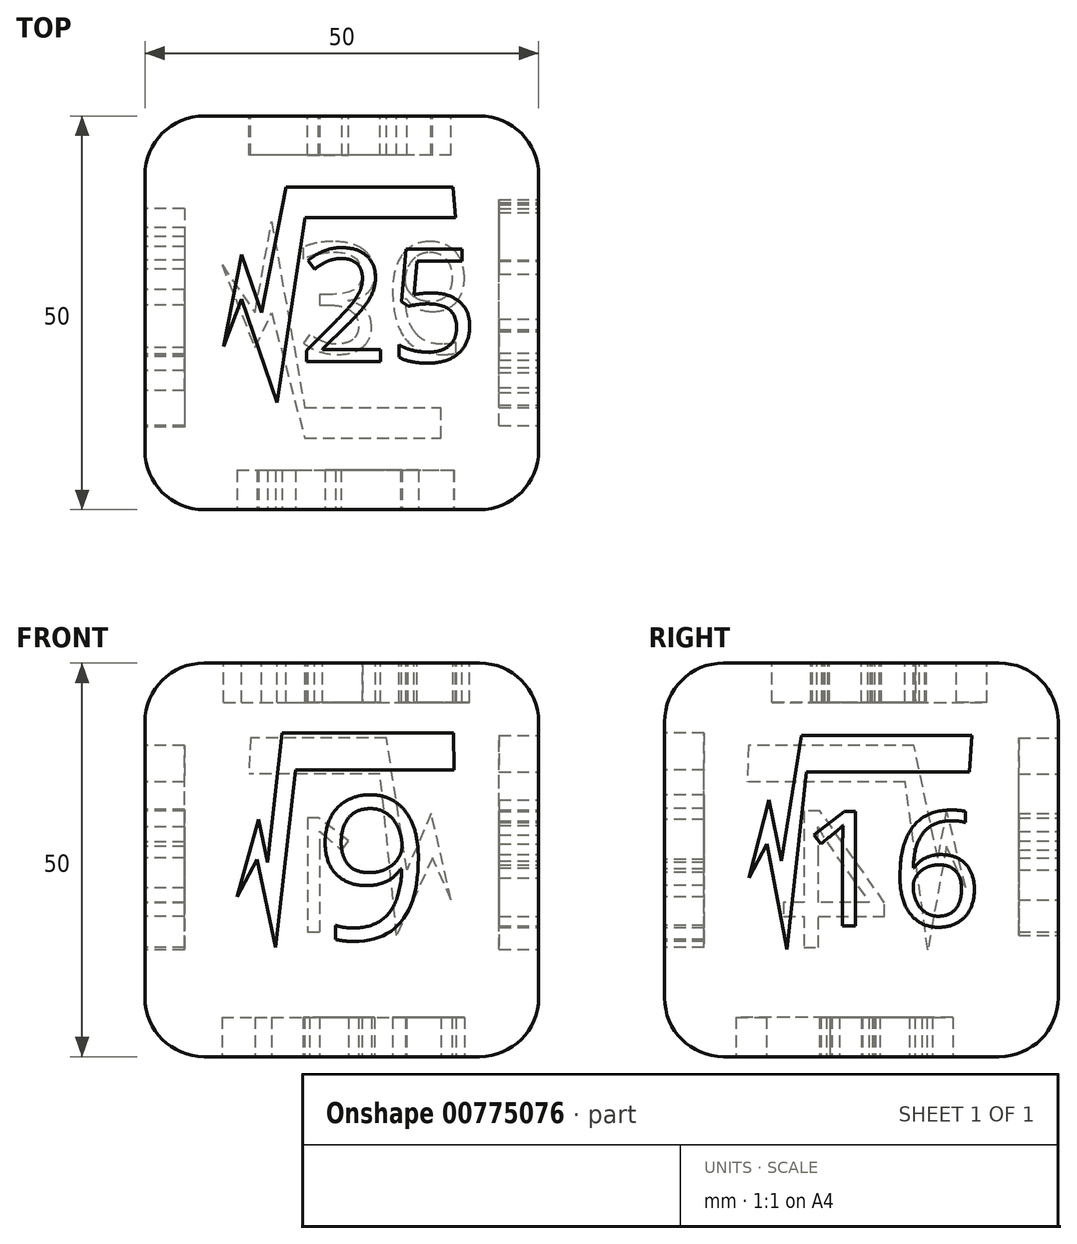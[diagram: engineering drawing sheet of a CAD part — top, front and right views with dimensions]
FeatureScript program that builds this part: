
annotation { "Feature Type Name" : "Feature", "Feature Type Description" : "" }
export const myFeature = defineFeature(function(context is Context, id is Id, definition is map)
    precondition{}
    {
        {
            var Q0;
            Q0=qCreatedBy(makeId("Top.planeOp"),FACE);
            var sketch = newSketch(context, id + "F0", { "sketchPlane" : qUnion([Q0])});
            skLineSegment(sketch, "E0.bottom", {"start": v(-25, 25) * mm, "end": v(25, 25) * mm});
            skLineSegment(sketch, "E0.top", {"start": v(-25, -25) * mm, "end": v(25, -25) * mm});
            skLineSegment(sketch, "E0.left", {"start": v(-25, 25) * mm, "end": v(-25, -25) * mm});
            skLineSegment(sketch, "E0.right", {"start": v(25, 25) * mm, "end": v(25, -25) * mm});
            skPoint(sketch, "E0.middle", {"position": v(0, 0) * mm});
            skSolve(sketch);
        }
        {
            var Q0;
            Q0 = qSketchRegion(id + "F0", true);
            extrude(context, id + "F1", {"entities" : qUnion([Q0]), "depth" : 50 * mm, "offsetDistance" : 25 * mm});
        }
        {
            var Q0;
            Q0=makeQuery(id+"F1.opExtrude","CAP_EDGE",EDGE,{"disambiguationData":[OSD([sQuery(id+"F0.wireOp",EDGE,"E0.left")])],"isStart":false});
            var Q1;
            Q1=makeQuery(id+"F1.opExtrude","CAP_EDGE",EDGE,{"disambiguationData":[OSD([sQuery(id+"F0.wireOp",EDGE,"E0.top")])],"isStart":false});
            var Q2;
            Q2=makeQuery(id+"F1.opExtrude","CAP_EDGE",EDGE,{"disambiguationData":[OSD([sQuery(id+"F0.wireOp",EDGE,"E0.right")])],"isStart":false});
            var Q3;
            Q3=makeQuery(id+"F1.opExtrude","CAP_EDGE",EDGE,{"disambiguationData":[OSD([sQuery(id+"F0.wireOp",EDGE,"E0.bottom")])],"isStart":false});
            var Q4;
            Q4=makeQuery(id+"F1.opExtrude","CAP_EDGE",EDGE,{"disambiguationData":[OSD([sQuery(id+"F0.wireOp",EDGE,"E0.left")])],"isStart":true});
            var Q5;
            Q5=makeQuery(id+"F1.opExtrude","CAP_EDGE",EDGE,{"disambiguationData":[OSD([sQuery(id+"F0.wireOp",EDGE,"E0.top")])],"isStart":true});
            var Q6;
            Q6=makeQuery(id+"F1.opExtrude","CAP_EDGE",EDGE,{"disambiguationData":[OSD([sQuery(id+"F0.wireOp",EDGE,"E0.right")])],"isStart":true});
            var Q7;
            Q7=makeQuery(id+"F1.opExtrude","CAP_EDGE",EDGE,{"disambiguationData":[OSD([sQuery(id+"F0.wireOp",EDGE,"E0.bottom")])],"isStart":true});
            var Q8;
            Q8=makeQuery(id+"F1.opExtrude","SWEPT_EDGE",EDGE,{"disambiguationData":[OSD([sQuery(id+"F0.wireOp",EDGE,"E0.bottom"),sQuery(id+"F0.wireOp",EDGE,"E0.left")])]});
            var Q9;
            Q9=makeQuery(id+"F1.opExtrude","SWEPT_EDGE",EDGE,{"disambiguationData":[OSD([sQuery(id+"F0.wireOp",EDGE,"E0.top"),sQuery(id+"F0.wireOp",EDGE,"E0.left")])]});
            var Q10;
            Q10=makeQuery(id+"F1.opExtrude","SWEPT_EDGE",EDGE,{"disambiguationData":[OSD([sQuery(id+"F0.wireOp",EDGE,"E0.top"),sQuery(id+"F0.wireOp",EDGE,"E0.right")])]});
            var Q11;
            Q11=makeQuery(id+"F1.opExtrude","SWEPT_EDGE",EDGE,{"disambiguationData":[OSD([sQuery(id+"F0.wireOp",EDGE,"E0.bottom"),sQuery(id+"F0.wireOp",EDGE,"E0.right")])]});
            fillet(context, id + "F2", {"entities" : qUnion([Q0, Q1, Q2, Q3, Q4, Q5, Q6, Q7, Q8, Q9, Q10, Q11]), "radius" : 7.5 * mm, "tangentPropagation" : true, "allowEdgeOverflow" : false});
        }
        {
            var Q0;
            Q0=makeQuery(id+"F1.opExtrude","SWEPT_FACE",FACE,{"disambiguationData":[OSD([sQuery(id+"F0.wireOp",EDGE,"E0.bottom")])]});
            var sketch = newSketch(context, id + "F3", { "sketchPlane" : qUnion([Q0])});
            skLineSegment(sketch, "E1", {"start": v(-13.9, 19.91) * mm, "end": v(-11.55, 25.25) * mm});
            skLineSegment(sketch, "E2", {"start": v(-11.55, 25.25) * mm, "end": v(-6.97, 15.38) * mm});
            skLineSegment(sketch, "E3", {"start": v(-6.97, 15.38) * mm, "end": v(-4.88, 35.9) * mm});
            skLineSegment(sketch, "E4", {"start": v(-4.88, 35.9) * mm, "end": v(11.8, 35.9) * mm});
            skText(sketch, "E5", { "text": "1", "fontName": "OpenSans-Regular.ttf"});
            skLineSegment(sketch, "E6", {"start": v(-13.9, 19.91) * mm, "end": v(-11.36, 30.9) * mm});
            skLineSegment(sketch, "E7", {"start": v(-11.36, 30.9) * mm, "end": v(-8.27, 23.7) * mm});
            skLineSegment(sketch, "E8", {"start": v(-8.27, 23.7) * mm, "end": v(-5.68, 40.49) * mm});
            skLineSegment(sketch, "E9", {"start": v(-5.68, 40.49) * mm, "end": v(11.6, 40.49) * mm});
            skLineSegment(sketch, "E10", {"start": v(11.6, 40.49) * mm, "end": v(11.8, 35.9) * mm});
            const initialGuessF3  = {"E5": [-0.00276, 0.01584, 1, 0, 0.01464]};
            skSetInitialGuess(sketch, initialGuessF3);
            skSolve(sketch);
        }
        {
            var Q0;
            Q0=makeQuery(id+"F1.opExtrude","SWEPT_FACE",FACE,{"disambiguationData":[OSD([sQuery(id+"F0.wireOp",EDGE,"E0.left")])]});
            var sketch = newSketch(context, id + "F4", { "sketchPlane" : qUnion([Q0])});
            skLineSegment(sketch, "E11", {"start": v(-13.26, 21.43) * mm, "end": v(-10.81, 26.7) * mm});
            skLineSegment(sketch, "E12", {"start": v(-10.81, 26.7) * mm, "end": v(-8.43, 13.59) * mm});
            skLineSegment(sketch, "E13", {"start": v(-8.43, 13.59) * mm, "end": v(-5.57, 34.93) * mm});
            skLineSegment(sketch, "E14", {"start": v(-5.57, 34.93) * mm, "end": v(14.54, 34.93) * mm});
            skText(sketch, "E15", { "text": "4", "fontName": "OpenSans-Regular.ttf"});
            skLineSegment(sketch, "E16", {"start": v(-13.26, 21.43) * mm, "end": v(-10.81, 31.41) * mm});
            skLineSegment(sketch, "E17", {"start": v(-10.81, 31.41) * mm, "end": v(-9.7, 25.27) * mm});
            skLineSegment(sketch, "E18", {"start": v(-9.7, 25.27) * mm, "end": v(-6.7, 39.53) * mm});
            skLineSegment(sketch, "E19", {"start": v(-6.7, 39.53) * mm, "end": v(14.3, 39.53) * mm});
            skLineSegment(sketch, "E20", {"start": v(14.3, 39.53) * mm, "end": v(14.54, 34.93) * mm});
            const initialGuessF4  = {"E15": [-0.00345, 0.01388, 1, 0, 0.01738]};
            skSetInitialGuess(sketch, initialGuessF4);
            skSolve(sketch);
        }
        {
            var Q0;
            Q0=makeQuery(id+"F1.opExtrude","SWEPT_FACE",FACE,{"disambiguationData":[OSD([sQuery(id+"F0.wireOp",EDGE,"E0.top")])]});
            var sketch = newSketch(context, id + "F5", { "sketchPlane" : qUnion([Q0])});
            skLineSegment(sketch, "E21", {"start": v(-13.3, 20.28) * mm, "end": v(-10.77, 25.05) * mm});
            skLineSegment(sketch, "E22", {"start": v(-10.77, 25.05) * mm, "end": v(-8.42, 13.88) * mm});
            skLineSegment(sketch, "E23", {"start": v(-8.42, 13.88) * mm, "end": v(-5.85, 36.44) * mm});
            skLineSegment(sketch, "E24", {"start": v(-5.85, 36.44) * mm, "end": v(14.22, 36.44) * mm});
            skText(sketch, "E25", { "text": "9", "fontName": "OpenSans-Regular.ttf"});
            skLineSegment(sketch, "E26", {"start": v(-13.3, 20.28) * mm, "end": v(-10.57, 30.14) * mm});
            skLineSegment(sketch, "E27", {"start": v(-10.57, 30.14) * mm, "end": v(-9.43, 24.69) * mm});
            skLineSegment(sketch, "E28", {"start": v(-9.43, 24.69) * mm, "end": v(-7.56, 41.1) * mm});
            skLineSegment(sketch, "E29", {"start": v(-7.56, 41.1) * mm, "end": v(14.18, 41.1) * mm});
            skLineSegment(sketch, "E30", {"start": v(14.18, 41.1) * mm, "end": v(14.22, 36.44) * mm});
            const initialGuessF5  = {"E25": [-0.00342, 0.0149, 1, 0, 0.01827]};
            skSetInitialGuess(sketch, initialGuessF5);
            skSolve(sketch);
        }
        {
            var Q0;
            Q0=makeQuery(id+"F1.opExtrude","SWEPT_FACE",FACE,{"disambiguationData":[OSD([sQuery(id+"F0.wireOp",EDGE,"E0.right")])]});
            var sketch = newSketch(context, id + "F6", { "sketchPlane" : qUnion([Q0])});
            skLineSegment(sketch, "E31", {"start": v(-14.3, 22.7) * mm, "end": v(-12.01, 27.05) * mm});
            skLineSegment(sketch, "E32", {"start": v(-12.01, 27.05) * mm, "end": v(-9.47, 13.62) * mm});
            skLineSegment(sketch, "E33", {"start": v(-9.47, 13.62) * mm, "end": v(-6.96, 36.2) * mm});
            skLineSegment(sketch, "E34", {"start": v(-6.96, 36.2) * mm, "end": v(13.73, 36.2) * mm});
            skText(sketch, "E35", { "text": "16", "fontName": "OpenSans-Regular.ttf"});
            skLineSegment(sketch, "E36", {"start": v(-14.3, 22.7) * mm, "end": v(-11.73, 32.62) * mm});
            skLineSegment(sketch, "E37", {"start": v(-11.73, 32.62) * mm, "end": v(-10.15, 24.9) * mm});
            skLineSegment(sketch, "E38", {"start": v(-10.15, 24.9) * mm, "end": v(-7.6, 40.83) * mm});
            skLineSegment(sketch, "E39", {"start": v(-7.6, 40.83) * mm, "end": v(14.02, 40.83) * mm});
            skLineSegment(sketch, "E40", {"start": v(14.02, 40.83) * mm, "end": v(13.73, 36.2) * mm});
            const initialGuessF6  = {"E35": [-0.00786, 0.01664, 1, 0, 0.01461]};
            skSetInitialGuess(sketch, initialGuessF6);
            skSolve(sketch);
        }
        {
            var Q0;
            Q0=makeQuery(id+"F1.opExtrude","CAP_FACE",FACE,{"disambiguationData":[OSD([sQuery(id+"F0.wireOp",EDGE,"E0.bottom"),sQuery(id+"F0.wireOp",EDGE,"E0.top"),sQuery(id+"F0.wireOp",EDGE,"E0.left"),sQuery(id+"F0.wireOp",EDGE,"E0.right")])],"isStart":false});
            var sketch = newSketch(context, id + "F7", { "sketchPlane" : qUnion([Q0])});
            skLineSegment(sketch, "E41", {"start": v(-15.02, -4.26) * mm, "end": v(-12.76, 1.73) * mm});
            skLineSegment(sketch, "E42", {"start": v(-12.76, 1.73) * mm, "end": v(-8.22, -11.39) * mm});
            skLineSegment(sketch, "E43", {"start": v(-8.22, -11.39) * mm, "end": v(-4.66, 12.09) * mm});
            skLineSegment(sketch, "E44", {"start": v(-4.66, 12.09) * mm, "end": v(14.42, 12.09) * mm});
            skLineSegment(sketch, "E45", {"start": v(-15.02, -4.26) * mm, "end": v(-12.76, 7.4) * mm});
            skLineSegment(sketch, "E46", {"start": v(-12.76, 7.4) * mm, "end": v(-10.2, 0) * mm});
            skLineSegment(sketch, "E47", {"start": v(-10.2, 0) * mm, "end": v(-7.1, 15.95) * mm});
            skLineSegment(sketch, "E48", {"start": v(-7.1, 15.95) * mm, "end": v(14.11, 15.95) * mm});
            skLineSegment(sketch, "E49", {"start": v(14.11, 15.95) * mm, "end": v(14.42, 12.09) * mm});
            skText(sketch, "E50", { "text": "25", "fontName": "OpenSans-Regular.ttf"});
            const initialGuessF7  = {"E50": [-0.00547, -0.0062, 1, 0, 0.0144]};
            skSetInitialGuess(sketch, initialGuessF7);
            skSolve(sketch);
        }
        {
            var Q0;
            Q0=makeQuery(id+"F1.opExtrude","CAP_FACE",FACE,{"disambiguationData":[OSD([sQuery(id+"F0.wireOp",EDGE,"E0.bottom"),sQuery(id+"F0.wireOp",EDGE,"E0.top"),sQuery(id+"F0.wireOp",EDGE,"E0.left"),sQuery(id+"F0.wireOp",EDGE,"E0.right")])],"isStart":true});
            var sketch = newSketch(context, id + "F8", { "sketchPlane" : qUnion([Q0])});
            skLineSegment(sketch, "E51", {"start": v(-15.23, -6.1) * mm, "end": v(-11.02, 0) * mm});
            skLineSegment(sketch, "E52", {"start": v(-11.02, 0) * mm, "end": v(-8.92, -11.6) * mm});
            skLineSegment(sketch, "E53", {"start": v(-8.92, -11.6) * mm, "end": v(-4.7, 12.02) * mm});
            skLineSegment(sketch, "E54", {"start": v(-4.7, 12.02) * mm, "end": v(12.61, 12.02) * mm});
            skLineSegment(sketch, "E55", {"start": v(-15.23, -6.1) * mm, "end": v(-11.02, 4.42) * mm});
            skLineSegment(sketch, "E56", {"start": v(-11.02, 4.42) * mm, "end": v(-8.92, 0) * mm});
            skLineSegment(sketch, "E57", {"start": v(-8.92, 0) * mm, "end": v(-4.7, 15.9) * mm});
            skLineSegment(sketch, "E58", {"start": v(-4.7, 15.9) * mm, "end": v(12.61, 15.9) * mm});
            skLineSegment(sketch, "E59", {"start": v(12.61, 15.9) * mm, "end": v(12.61, 12.02) * mm});
            skText(sketch, "E60", { "text": "36", "fontName": "OpenSans-Regular.ttf"});
            const initialGuessF8  = {"E60": [-0.00584, -0.00886, 1, 0, 0.01408]};
            skSetInitialGuess(sketch, initialGuessF8);
            skSolve(sketch);
        }
        {
            var Q0;
            Q0 = qSketchRegion(id + "F3", true);
            extrude(context, id + "F9", {"entities" : qUnion([Q0]), "operationType" : NewBodyOperationType.REMOVE, "oppositeDirection" : true, "depth" : 5 * mm, "offsetDistance" : 25 * mm});
        }
        {
            var Q0;
            Q0 = qSketchRegion(id + "F4", true);
            extrude(context, id + "F10", {"entities" : qUnion([Q0]), "operationType" : NewBodyOperationType.REMOVE, "oppositeDirection" : true, "depth" : 5 * mm, "offsetDistance" : 25 * mm});
        }
        {
            var Q0;
            Q0 = qSketchRegion(id + "F5", true);
            extrude(context, id + "F11", {"entities" : qUnion([Q0]), "operationType" : NewBodyOperationType.REMOVE, "oppositeDirection" : true, "depth" : 5 * mm, "offsetDistance" : 25 * mm});
        }
        {
            var Q0;
            Q0 = qSketchRegion(id + "F6", true);
            extrude(context, id + "F12", {"entities" : qUnion([Q0]), "operationType" : NewBodyOperationType.REMOVE, "oppositeDirection" : true, "depth" : 5 * mm, "offsetDistance" : 25 * mm});
        }
        {
            var Q0;
            Q0 = qSketchRegion(id + "F7", true);
            extrude(context, id + "F13", {"entities" : qUnion([Q0]), "operationType" : NewBodyOperationType.REMOVE, "oppositeDirection" : true, "depth" : 5 * mm, "offsetDistance" : 25 * mm});
        }
        {
            var Q0;
            Q0 = qSketchRegion(id + "F8", true);
            extrude(context, id + "F14", {"entities" : qUnion([Q0]), "operationType" : NewBodyOperationType.REMOVE, "oppositeDirection" : true, "depth" : 5 * mm, "offsetDistance" : 25 * mm});
        }
    });
